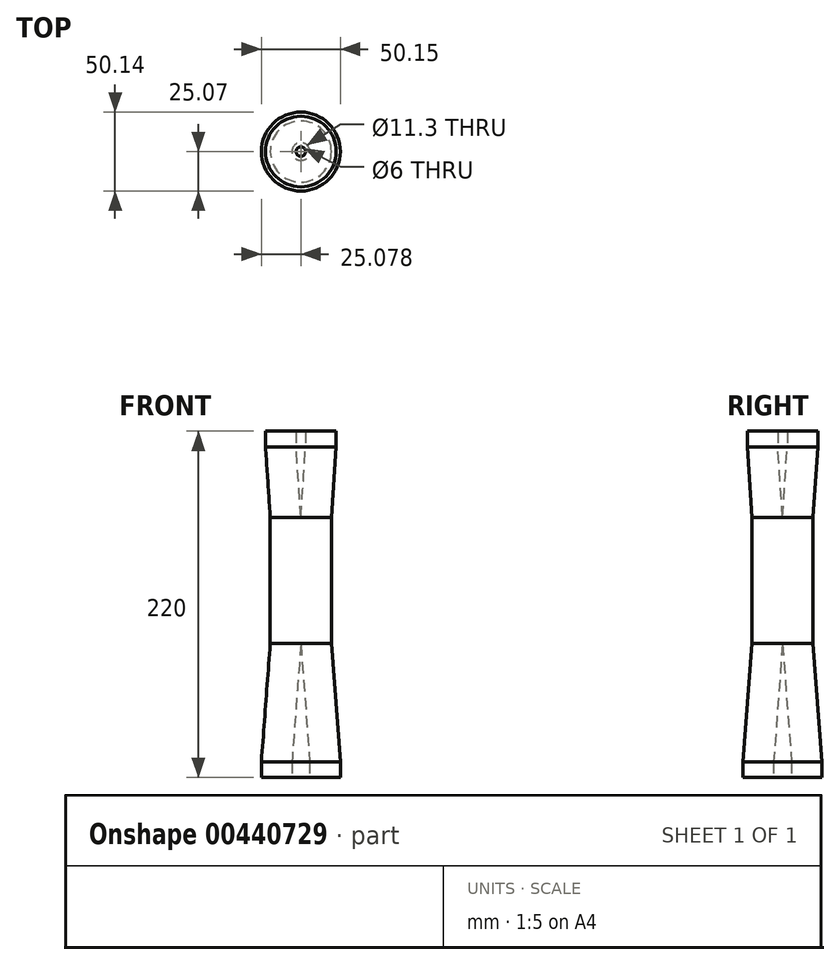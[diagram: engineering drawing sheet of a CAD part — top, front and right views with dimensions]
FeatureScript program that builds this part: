
annotation { "Feature Type Name" : "Feature", "Feature Type Description" : "" }
export const myFeature = defineFeature(function(context is Context, id is Id, definition is map)
    precondition{}
    {
        {
            var Q0;
            Q0=qCreatedBy(makeId("Front.planeOp"),FACE);
            var sketch = newSketch(context, id + "F0", { "sketchPlane" : qUnion([Q0])});
            skLineSegment(sketch, "E0", {"start": v(-42.1, 112.7) * mm, "end": v(-42.1, 102.7) * mm});
            skLineSegment(sketch, "E1", {"start": v(-42.1, 102.7) * mm, "end": v(-39.1, 57.7) * mm});
            skLineSegment(sketch, "E2", {"start": v(-39.1, 57.7) * mm, "end": v(-39.1, -22.3) * mm});
            skLineSegment(sketch, "E3", {"start": v(-39.1, -22.3) * mm, "end": v(-44.76, -97.3) * mm});
            skLineSegment(sketch, "E4", {"start": v(-44.76, -97.3) * mm, "end": v(-44.76, -107.3) * mm});
            skLineSegment(sketch, "E5", {"start": v(-44.76, -107.3) * mm, "end": v(-25.33, -107.3) * mm});
            skLineSegment(sketch, "E6", {"start": v(-25.33, -97.3) * mm, "end": v(-25.33, -107.3) * mm});
            skLineSegment(sketch, "E7", {"start": v(-25.33, -97.3) * mm, "end": v(-19.68, -22.3) * mm});
            skLineSegment(sketch, "E8", {"start": v(-19.68, -22.3) * mm, "end": v(-19.68, 57.7) * mm});
            skLineSegment(sketch, "E9", {"start": v(-19.68, 57.7) * mm, "end": v(-22.68, 102.7) * mm});
            skLineSegment(sketch, "E10", {"start": v(-22.68, 102.7) * mm, "end": v(-22.68, 112.7) * mm});
            skLineSegment(sketch, "E11", {"start": v(-22.68, 112.7) * mm, "end": v(-42.1, 112.7) * mm});
            skPoint(sketch, "E12", {"position": v(-25.33, -107.3) * mm});
            skSolve(sketch);
        }
        {
            var Q0;
            Q0=makeQuery(id+"F0.imprint","IMPRINT",FACE,{"disambiguationData":[TD([[makeQuery(id+"F0.imprint","IMPRINT",EDGE,{"derivedFrom":sQuery(id+"F0.wireOp",EDGE,"E0")}),1.0]])]});
            var Q1;
            Q1=sQuery(id+"F0.wireOp",EDGE,"E8");
            revolve(context, id + "F1", {"entities" : qUnion([Q0]), "axis" : qUnion([Q1]), "revolveType" : RevolveType.FULL});
        }
    });
